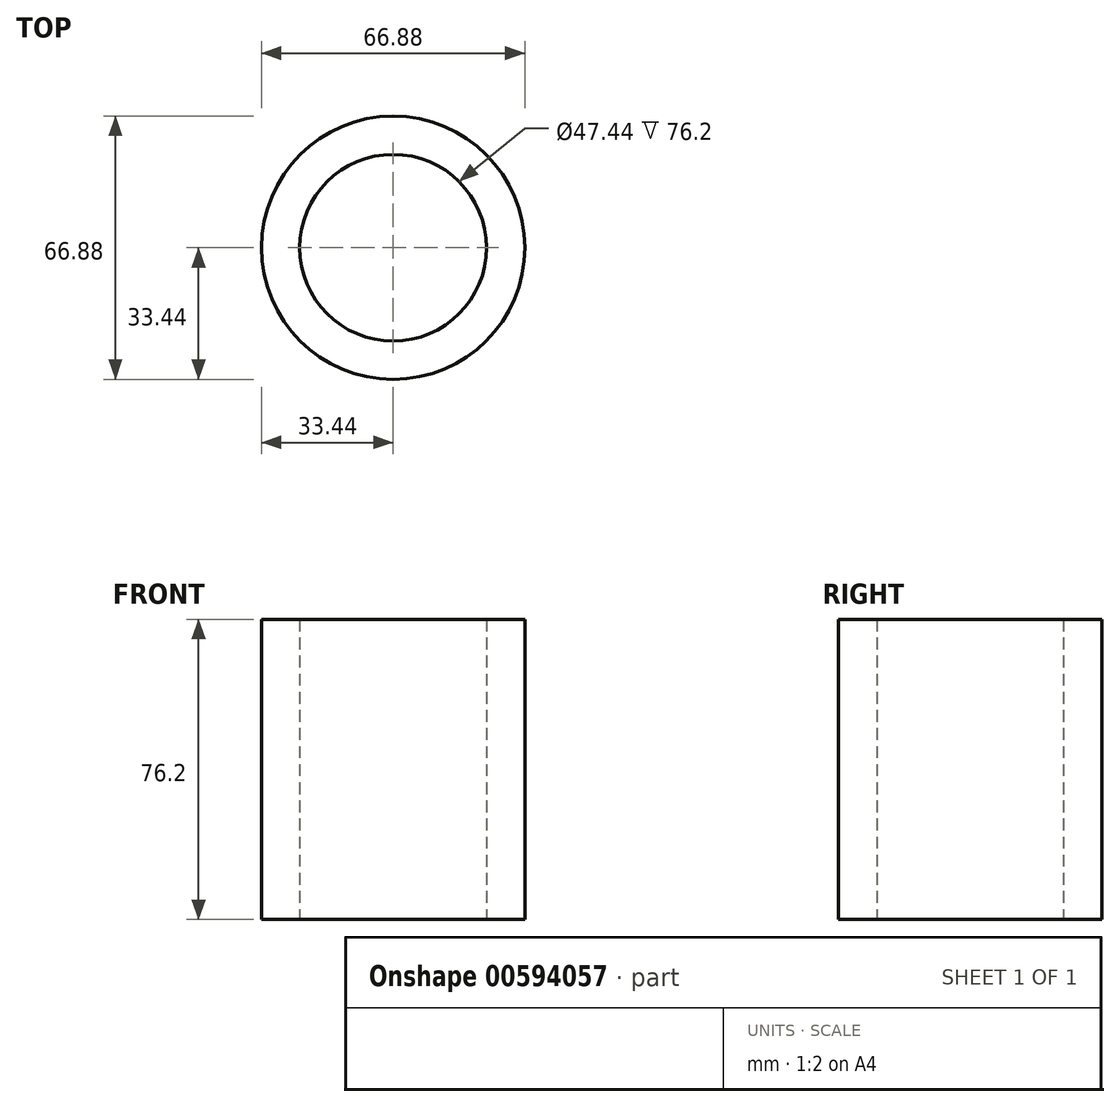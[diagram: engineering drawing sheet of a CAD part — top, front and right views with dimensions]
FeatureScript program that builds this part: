
annotation { "Feature Type Name" : "Feature", "Feature Type Description" : "" }
export const myFeature = defineFeature(function(context is Context, id is Id, definition is map)
    precondition{}
    {
        {
            var Q0;
            Q0=qCreatedBy(makeId("Top.planeOp"),FACE);
            var sketch = newSketch(context, id + "F0", { "sketchPlane" : qUnion([Q0])});
            skCircle(sketch, "E0", {"center": v(0, 0) * mm, "radius": 33.44 * mm});
            skCircle(sketch, "E1", {"center": v(0, 0) * mm, "radius": 23.72 * mm});
            skSolve(sketch);
        }
        {
            var Q0;
            Q0=makeQuery(id+"F0.imprint","IMPRINT",FACE,{"disambiguationData":[TD([[makeQuery(id+"F0.imprint","IMPRINT",EDGE,{"derivedFrom":sQuery(id+"F0.wireOp",EDGE,"E0")}),1.0]])]});
            extrude(context, id + "F1", {"entities" : qUnion([Q0]), "depth" : 76.2 * mm, "offsetDistance" : 25.4 * mm});
        }
    });
